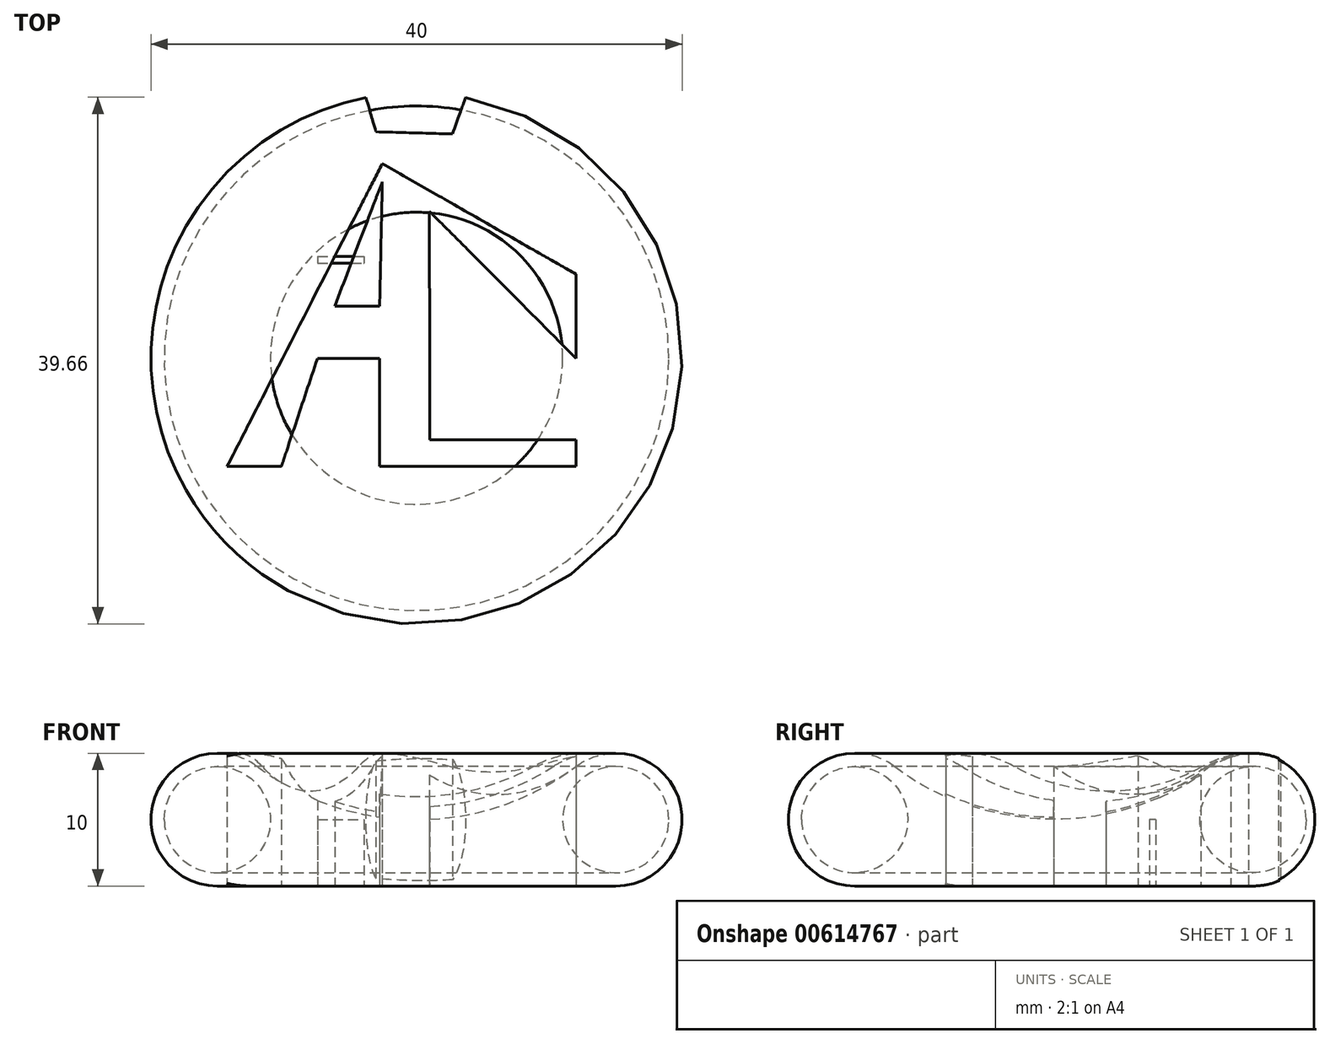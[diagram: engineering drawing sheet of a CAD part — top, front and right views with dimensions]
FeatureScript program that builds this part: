
annotation { "Feature Type Name" : "Feature", "Feature Type Description" : "" }
export const myFeature = defineFeature(function(context is Context, id is Id, definition is map)
    precondition{}
    {
        {
            var Q0;
            Q0=qCreatedBy(makeId("Front.planeOp"),FACE);
            var sketch = newSketch(context, id + "F0", { "sketchPlane" : qUnion([Q0])});
            skArc(sketch, "E0", {"start": v(-12, 9) * mm, "mid": v(-19.74, 6.58) * mm, "end": v(-15, 0) * mm});
            skArc(sketch, "E1", {"start": v(-12, 9) * mm, "mid": v(-6.32, 6.03) * mm, "end": v(0, 5) * mm});
            skLineSegment(sketch, "E2", {"start": v(0, 5) * mm, "end": v(0, 0) * mm});
            skLineSegment(sketch, "E3", {"start": v(0, 0) * mm, "end": v(-15, 0) * mm});
            skSolve(sketch);
        }
        {
            var Q0;
            Q0=makeQuery(id+"F0.imprint","IMPRINT",FACE,{"disambiguationData":[TD([[makeQuery(id+"F0.imprint","IMPRINT",EDGE,{"derivedFrom":sQuery(id+"F0.wireOp",EDGE,"E0")}),1.0]])]});
            var Q1;
            Q1=sQuery(id+"F0.wireOp",EDGE,"E2");
            revolve(context, id + "F1", {"entities" : qUnion([Q0]), "axis" : qUnion([Q1]), "revolveType" : RevolveType.FULL});
        }
        {
            var Q0;
            Q0=qCreatedBy(makeId("Top.planeOp"),FACE);
            var sketch = newSketch(context, id + "F2", { "sketchPlane" : qUnion([Q0])});
            skLineSegment(sketch, "E4", {"start": v(-2.58, -8.15) * mm, "end": v(4.1, -8.15) * mm});
            skLineSegment(sketch, "E5", {"start": v(4.1, -8.15) * mm, "end": v(12, -8.15) * mm});
            skLineSegment(sketch, "E6.right", {"start": v(12, 0) * mm, "end": v(12, 6.34) * mm});
            skLineSegment(sketch, "E7", {"start": v(12, 6.34) * mm, "end": v(-2.58, 14.66) * mm});
            skLineSegment(sketch, "E8.bottom", {"start": v(-10.18, -8.15) * mm, "end": v(-14.27, -8.15) * mm});
            skLineSegment(sketch, "E9", {"start": v(-14.27, -8.15) * mm, "end": v(-2.58, 14.66) * mm});
            skLineSegment(sketch, "E10", {"start": v(-10.18, -8.15) * mm, "end": v(-7.46, 0) * mm});
            skPoint(sketch, "E11.end.orphan", {"position": v(-2.48, 7.75) * mm});
            skLineSegment(sketch, "E12.bottom", {"start": v(-2.58, -8.15) * mm, "end": v(-2.78, -8.15) * mm});
            skLineSegment(sketch, "E12.right", {"start": v(-2.78, -8.15) * mm, "end": v(-2.78, 0) * mm});
            skPoint(sketch, "E12.top.end.orphan", {"position": v(-2.78, 14.66) * mm});
            skPoint(sketch, "E13.orphan", {"position": v(-6.38, 3.25) * mm});
            skPoint(sketch, "E14.end.orphan", {"position": v(4.7, 7.23) * mm});
            skLineSegment(sketch, "E15.bottom", {"start": v(4.1, -8.15) * mm, "end": v(3.9, -8.15) * mm});
            skPoint(sketch, "E16.start.orphan", {"position": v(-2.58, 3.25) * mm});
            skLineSegment(sketch, "E17.bottom", {"start": v(-2.58, -8.15) * mm, "end": v(4.12, -8.15) * mm});
            skLineSegment(sketch, "E18", {"start": v(12, -7.95) * mm, "end": v(12, -8.15) * mm});
            skLineSegment(sketch, "E19.bottom", {"start": v(-14.27, -8.15) * mm, "end": v(-10.18, -8.15) * mm});
            skLineSegment(sketch, "E19.top", {"start": v(-13.97, -7.95) * mm, "end": v(-10.31, -7.95) * mm});
            skPoint(sketch, "E19.left.end.orphan", {"position": v(-14.27, -7.95) * mm});
            skPoint(sketch, "E20.orphan", {"position": v(-10.38, -8.15) * mm});
            skPoint(sketch, "E21.orphan", {"position": v(-14.07, -8.15) * mm});
            skPoint(sketch, "E22.orphan", {"position": v(11.82, 6.44) * mm});
            skPoint(sketch, "E23.orphan", {"position": v(12, 6.14) * mm});
            skPoint(sketch, "E24.orphan", {"position": v(12, 0) * mm});
            skLineSegment(sketch, "E25", {"start": v(-2.58, 3.05) * mm, "end": v(-2.58, 3.25) * mm});
            skLineSegment(sketch, "E26.top", {"start": v(4.13, -6.15) * mm, "end": v(12, -6.15) * mm});
            skLineSegment(sketch, "E26.right", {"start": v(12, -8.15) * mm, "end": v(12, -6.15) * mm});
            skLineSegment(sketch, "E27", {"start": v(-6.16, 3.91) * mm, "end": v(-2.78, 3.91) * mm});
            skPoint(sketch, "E17.top.start.orphan", {"position": v(-2.58, -7.95) * mm});
            skLineSegment(sketch, "E28.bottom", {"start": v(4.1, -8.15) * mm, "end": v(2.1, -8.15) * mm});
            skPoint(sketch, "E29.orphan", {"position": v(4.1, 11.99) * mm});
            skLineSegment(sketch, "E30", {"start": v(12, 0) * mm, "end": v(4.1, 7.94) * mm});
            skPoint(sketch, "E31.orphan", {"position": v(12, -0.2) * mm});
            skPoint(sketch, "E28.right.end.orphan", {"position": v(2.1, 11.99) * mm});
            skLineSegment(sketch, "E32", {"start": v(1, -6.15) * mm, "end": v(0.98, 7.94) * mm});
            skLineSegment(sketch, "E33", {"start": v(-7.46, 0) * mm, "end": v(-2.78, 0) * mm});
            skLineSegment(sketch, "E34", {"start": v(-6.16, 3.91) * mm, "end": v(-2.58, 13.3) * mm});
            skLineSegment(sketch, "E35", {"start": v(-2.58, 13.3) * mm, "end": v(-2.78, 3.91) * mm});
            skLineSegment(sketch, "E36", {"start": v(4.13, -6.15) * mm, "end": v(1, -6.15) * mm});
            skLineSegment(sketch, "E37", {"start": v(0.98, 7.94) * mm, "end": v(0.98, 11.06) * mm});
            skLineSegment(sketch, "E38", {"start": v(4.1, 7.94) * mm, "end": v(0.98, 11.06) * mm});
            skSolve(sketch);
        }
        {
            var Q0;
            Q0 = qSketchRegion(id + "F2", true);
            extrude(context, id + "F3", {"entities" : qUnion([Q0]), "operationType" : NewBodyOperationType.REMOVE, "depth" : 25 * mm, "offsetDistance" : 25 * mm});
        }
        {
            var Q0;
            Q0=qCreatedBy(makeId("Top.planeOp"),FACE);
            var sketch = newSketch(context, id + "F4", { "sketchPlane" : qUnion([Q0])});
            skCircle(sketch, "E39.cCircle", {"center": v(-0.06, 20.95) * mm, "radius": 3.97 * mm, "construction": true});
            skLineSegment(sketch, "E39.0", {"start": v(4.65, 22.33) * mm, "end": v(2.71, 16.9) * mm});
            skLineSegment(sketch, "E39.1", {"start": v(2.71, 16.9) * mm, "end": v(-3.05, 17.06) * mm});
            skLineSegment(sketch, "E39.2", {"start": v(-3.05, 17.06) * mm, "end": v(-4.68, 22.6) * mm});
            skLineSegment(sketch, "E39.3", {"start": v(-4.68, 22.6) * mm, "end": v(0.07, 25.85) * mm});
            skLineSegment(sketch, "E39.4", {"start": v(0.07, 25.85) * mm, "end": v(4.65, 22.33) * mm});
            skPoint(sketch, "E39.0.midPoint", {"position": v(3.68, 19.62) * mm});
            skSolve(sketch);
        }
        {
            var Q0;
            Q0 = qSketchRegion(id + "F4", true);
            extrude(context, id + "F5", {"entities" : qUnion([Q0]), "operationType" : NewBodyOperationType.REMOVE, "depth" : 25 * mm, "offsetDistance" : 25 * mm});
        }
        {
            var Q0;
            Q0=qCreatedBy(makeId("Front.planeOp"),FACE);
            var sketch = newSketch(context, id + "F6", { "sketchPlane" : qUnion([Q0])});
            skCircle(sketch, "E40", {"center": v(-15, 5) * mm, "radius": 4 * mm});
            skSolve(sketch);
        }
        {
            var Q0;
            Q0 = qSketchRegion(id + "F6", true);
            var Q1;
            Q1=makeQuery(id+"F5HIMYaS0rjiIXQ_1.4.F5.boolean.opBoolean","COPY",FACE,{"derivedFrom":makeQuery(id+"F5HIMYaS0rjiIXQ_1.4.F5.opExtrude","SWEPT_FACE",FACE,{"disambiguationData":[OSD([sQuery(id+"F4.wireOp",EDGE,"E39.1")])]})});
            var Q2;
            Q2=sQuery(id+"F0.wireOp",EDGE,"E2");
            revolve(context, id + "F7", {"entities" : qUnion([Q0, Q1]), "axis" : qUnion([Q2]), "revolveType" : RevolveType.FULL});
        }
        {
            var Q0;
            Q0=qCreatedBy(makeId("Top.planeOp"),FACE);
            var sketch = newSketch(context, id + "F8", { "sketchPlane" : qUnion([Q0])});
            skLineSegment(sketch, "E41.bottom", {"start": v(-7.45, 7.68) * mm, "end": v(-3.95, 7.68) * mm});
            skLineSegment(sketch, "E41.top", {"start": v(-7.45, 7.18) * mm, "end": v(-3.95, 7.18) * mm});
            skLineSegment(sketch, "E41.left", {"start": v(-7.45, 7.68) * mm, "end": v(-7.45, 7.18) * mm});
            skLineSegment(sketch, "E41.right", {"start": v(-3.95, 7.68) * mm, "end": v(-3.95, 7.18) * mm});
            skSolve(sketch);
        }
        {
            var Q0;
            Q0 = qSketchRegion(id + "F8", true);
            extrude(context, id + "F9", {"entities" : qUnion([Q0]), "depth" : 5 * mm, "offsetDistance" : 25 * mm});
        }
    });
